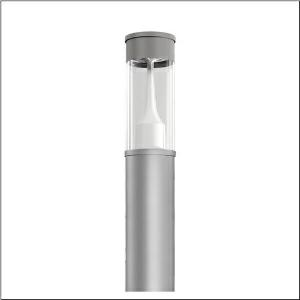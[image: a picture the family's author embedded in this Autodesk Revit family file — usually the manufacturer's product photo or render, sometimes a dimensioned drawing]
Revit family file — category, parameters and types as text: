
# Revit family: city-light_400_iq___st1_2a_5xa5305af14hp_8cfd
name_source: partatom
category: Lighting Fixtures
units: mm (PartAtom-declared; Revit-internal decimal feet)

## family parameters
Cut with Voids When Loaded = No
Host = Face
Light Source = No
Part Type = Normal
Room Calculation Point = No
Round Connector Dimension = Use Diameter
Shared = No

## types (1)
- --- (1 x LED, 3910 lm, 33.6 W, 2200K)
    Apparent Load = 34 VA
    CIE Flux Codes = 22 61 94 96 100
    Color Rendering = 70
    Color Temperature = 2200K
    Default Elevation = 1800 mm
    Description = City-Light 400 iQ, light pillar, Module 540 iQ-SR, primary light control with 3 zone facetted reflector, of plastic, silver coated, highly specular, structured, primary optical cover: cover, of PMMA, transparent, partly coated, light distribution: ST1.2a, primary light characteristic: asymmetric, LED, High Power LED, rated luminous flux: 3.910lm, luminous efficacy: 116lm/W, light colour: 722, colour temperature: 2200K, control gear: ECG iQ, control: presetting dimming logarithmic, Street-Remote, Auto-Match, Temp-Guard, Lumen-Switch, Night-Set, Smart-Wire, Light-Fading, Desk-Remote (wireless, voltage-free reading and setting of iQ features in the workshop via application-optimized NFC function/RFID function), optimised constant luminous flux control (CLO 2.0), with terminal, 6-pole, max. 2.5mm², mains connection: 230..240V, AC, 50/60Hz, start of lifetime: 34W, end of service life: 36W, reduction: 15W, luminaire housing, cylindrical, of extruded aluminium section, coated, Siteco® metallic grey (DB 702S), length: 4.694mm, diameter: 200mm, Module 540 iQ-SR, traffic white (RAL 9016), equipment: Power, protection rating (complete): IP65, insulation class (complete): insulation class II (safety insulation), certification: CE, ENEC, VDE, packaging unit: 1 piece

Light Distribution: ST1.2a
    Height = 500 mm
    Lamp = 1 x LED
    Lamp Light Flux = 3910 lm
    Lamp Power = 33.6 W
    Lamp count = 1
    Length = 200 mm  [stored 0.656168 ft]
    Luminous efficacy = 116 lm/W
    Manufacturer = Siteco
    ModVariant = No
    Model = 5XA5305AF14HP
    Mounting Place = Floor
    Mounting Type = Freestanding
    Number of Poles = 1
    OnlyDefault = Yes
    Power Factor = 1
    Product Name = City-Light 400 iQ | ST1.2a
    Product group = light pillar
    ProductGroupID = 1303
    Protection Class = Protection class II
    Protection Degree = IP 65
    RLX_Detail_Level = 1
    RLX_Emergency_Light_Flux = 0 lm
    RLX_Emergency_Type = 0
    RLX_Emergency_Type_DB = No
    RlxData = <blob elided: 53081 chars, md5=4b46a8b3>
    Socket = socket
    Standby Power = 0 W
    System Light Flux = 3910 lm
    System Power = 34 W
    Type Comments = factory setting: luminous flux: 100 % | dim-lin: 254 | 695 mA
    Type Image = l_1006916.jpg
    URL = http://relux.com
    VarID = @adj_127335
    Voltage = 0 V
    Weight = 0.00 kg
    Width = 0 mm  [stored 0 ft]

note: [stored X ft] marks values corroborated as IEEE doubles in the binary element streams (Revit-internal decimal feet)

## geometry (parser evidence)
native form markers: Blend x4, Sweep x10
no freeform markers — native parametric forms only
